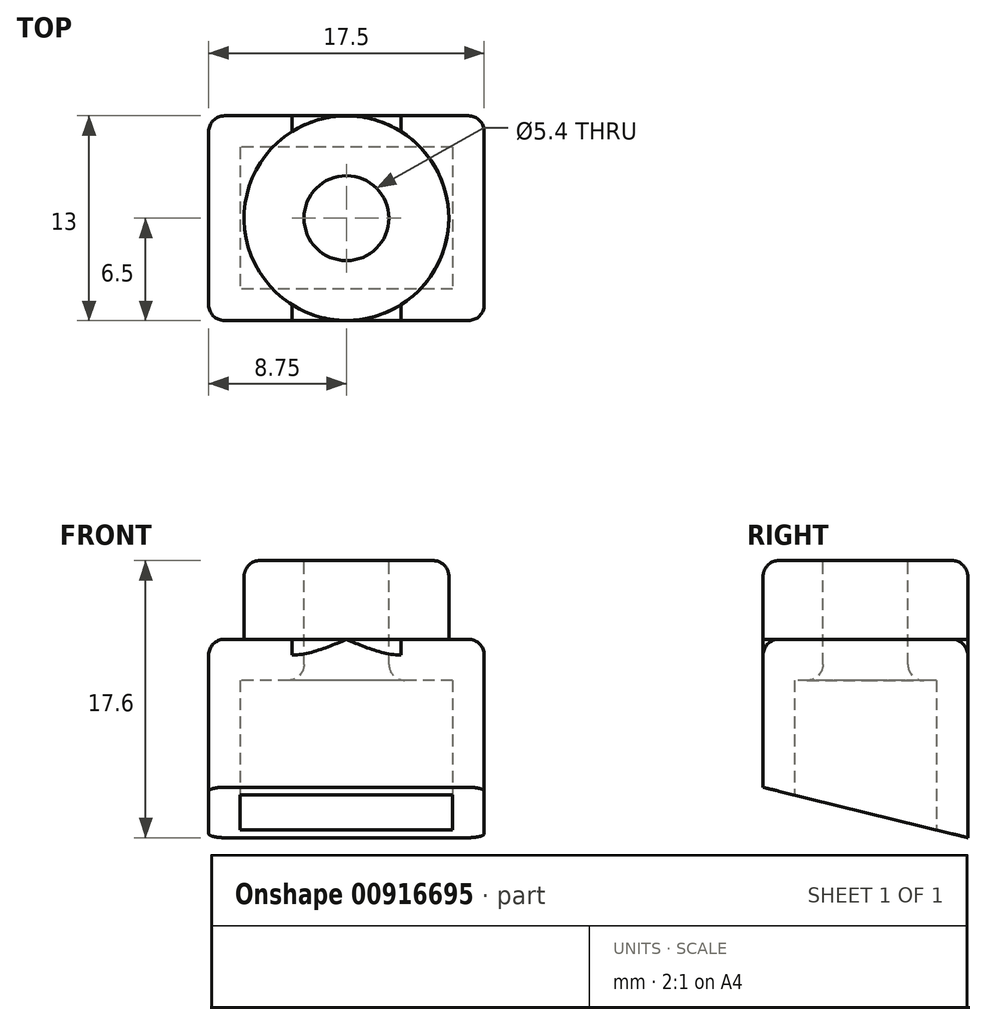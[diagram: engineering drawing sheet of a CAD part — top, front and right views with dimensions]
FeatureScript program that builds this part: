
annotation { "Feature Type Name" : "Feature", "Feature Type Description" : "" }
export const myFeature = defineFeature(function(context is Context, id is Id, definition is map)
    precondition{}
    {
        {
            var Q0;
            Q0=qCreatedBy(makeId("Top.planeOp"),FACE);
            var sketch = newSketch(context, id + "F0", { "sketchPlane" : qUnion([Q0])});
            skLineSegment(sketch, "E0.bottom", {"start": v(8.75, -6.5) * mm, "end": v(-8.75, -6.5) * mm});
            skLineSegment(sketch, "E0.top", {"start": v(8.75, 6.5) * mm, "end": v(-8.75, 6.5) * mm});
            skLineSegment(sketch, "E0.left", {"start": v(8.75, -6.5) * mm, "end": v(8.75, 6.5) * mm});
            skLineSegment(sketch, "E0.right", {"start": v(-8.75, -6.5) * mm, "end": v(-8.75, 6.5) * mm});
            skPoint(sketch, "E0.middle", {"position": v(0, 0) * mm});
            skSolve(sketch);
        }
        {
            var Q0;
            Q0 = qSketchRegion(id + "F0", true);
            extrude(context, id + "F1", {"entities" : qUnion([Q0]), "depth" : 12.6 * mm, "offsetDistance" : 25 * mm});
        }
        {
            var Q0;
            Q0=makeQuery(id+"F1.opExtrude","CAP_FACE",FACE,{"disambiguationData":[OSD([sQuery(id+"F0.wireOp",EDGE,"E0.bottom"),sQuery(id+"F0.wireOp",EDGE,"E0.top"),sQuery(id+"F0.wireOp",EDGE,"E0.left"),sQuery(id+"F0.wireOp",EDGE,"E0.right")])],"isStart":false});
            var sketch = newSketch(context, id + "F2", { "sketchPlane" : qUnion([Q0])});
            skCircle(sketch, "E1", {"center": v(0, 0) * mm, "radius": 6.5 * mm});
            skSolve(sketch);
        }
        {
            var Q0;
            Q0 = qSketchRegion(id + "F2", true);
            extrude(context, id + "F3", {"entities" : qUnion([Q0]), "operationType" : NewBodyOperationType.ADD, "depth" : 5 * mm, "offsetDistance" : 25 * mm});
        }
        {
            var Q0;
            Q0=makeQuery(id+"F1.opExtrude","SWEPT_FACE",FACE,{"disambiguationData":[OSD([sQuery(id+"F0.wireOp",EDGE,"E0.right")])]});
            var sketch = newSketch(context, id + "F4", { "sketchPlane" : qUnion([Q0])});
            skLineSegment(sketch, "E2", {"start": v(-6.5, 0) * mm, "end": v(6.5, 3.2) * mm});
            skLineSegment(sketch, "E3", {"start": v(6.5, 3.2) * mm, "end": v(6.5, 0) * mm});
            skLineSegment(sketch, "E4", {"start": v(6.5, 0) * mm, "end": v(-6.5, 0) * mm});
            skSolve(sketch);
        }
        {
            var Q0;
            Q0 = qSketchRegion(id + "F4", true);
            extrude(context, id + "F5", {"entities" : qUnion([Q0]), "operationType" : NewBodyOperationType.REMOVE, "endBound" : BoundingType.THROUGH_ALL, "oppositeDirection" : true, "depth" : 25 * mm, "offsetDistance" : 25 * mm});
        }
        {
            var Q0;
            Q0=makeQuery(id+"F3.opExtrude","CAP_FACE",FACE,{"disambiguationData":[OSD([sQuery(id+"F2.wireOp",EDGE,"E1")])],"isStart":false});
            var sketch = newSketch(context, id + "F6", { "sketchPlane" : qUnion([Q0])});
            skCircle(sketch, "E5", {"center": v(0, 0) * mm, "radius": 2.7 * mm});
            skSolve(sketch);
        }
        {
            var Q0;
            Q0 = qSketchRegion(id + "F6", true);
            extrude(context, id + "F7", {"entities" : qUnion([Q0]), "operationType" : NewBodyOperationType.REMOVE, "endBound" : BoundingType.THROUGH_ALL, "oppositeDirection" : true, "depth" : 25 * mm, "offsetDistance" : 25 * mm});
        }
        {
            var Q0;
            Q0=qCreatedBy(makeId("Top.planeOp"),FACE);
            var sketch = newSketch(context, id + "F8", { "sketchPlane" : qUnion([Q0])});
            skLineSegment(sketch, "E6.bottom", {"start": v(6.75, 4.5) * mm, "end": v(-6.75, 4.5) * mm});
            skLineSegment(sketch, "E6.top", {"start": v(6.75, -4.5) * mm, "end": v(-6.75, -4.5) * mm});
            skLineSegment(sketch, "E6.left", {"start": v(6.75, 4.5) * mm, "end": v(6.75, -4.5) * mm});
            skLineSegment(sketch, "E6.right", {"start": v(-6.75, 4.5) * mm, "end": v(-6.75, -4.5) * mm});
            skPoint(sketch, "E6.middle", {"position": v(0, 0) * mm});
            skSolve(sketch);
        }
        {
            var Q0;
            Q0 = qSketchRegion(id + "F8", true);
            extrude(context, id + "F9", {"entities" : qUnion([Q0]), "operationType" : NewBodyOperationType.REMOVE, "depth" : 10 * mm, "offsetDistance" : 25 * mm});
        }
        {
            var Q0;
            Q0=makeQuery(id+"F7.boolean.opBoolean","COPY",EDGE,{"derivedFrom":makeQuery(id+"F7.opExtrude","CAP_EDGE",EDGE,{"disambiguationData":[OSD([sQuery(id+"F6.wireOp",EDGE,"E5")])],"isStart":true})});
            var Q1;
            Q1=makeQuery(id+"F3.opExtrude","CAP_EDGE",EDGE,{"disambiguationData":[OSD([sQuery(id+"F2.wireOp",EDGE,"E1")])],"isStart":false});
            var Q2;
            {var subQ0=sQuery(id+"F0.wireOp",EDGE,"E0.right");var subQ1=sQuery(id+"F0.wireOp",EDGE,"E0.top");Q2=makeQuery(id+"F3.boolean.opBoolean","SPLIT",EDGE,{"disambiguationData":[TD([makeQuery(id+"F1.opExtrude","SWEPT_FACE",FACE,{"disambiguationData":[OSD([subQ0])]})])],"derivedFrom":makeQuery(id+"F1.opExtrude","CAP_EDGE",EDGE,{"disambiguationData":[OSD([subQ1])],"isStart":false})});}
            var Q3;
            Q3=makeQuery(id+"F1.opExtrude","CAP_EDGE",EDGE,{"disambiguationData":[OSD([sQuery(id+"F0.wireOp",EDGE,"E0.right")])],"isStart":false});
            var Q4;
            {var subQ0=sQuery(id+"F0.wireOp",EDGE,"E0.bottom");var subQ1=sQuery(id+"F0.wireOp",EDGE,"E0.right");Q4=makeQuery(id+"F3.boolean.opBoolean","SPLIT",EDGE,{"disambiguationData":[TD([makeQuery(id+"F1.opExtrude","SWEPT_FACE",FACE,{"disambiguationData":[OSD([subQ1])]})])],"derivedFrom":makeQuery(id+"F1.opExtrude","CAP_EDGE",EDGE,{"disambiguationData":[OSD([subQ0])],"isStart":false})});}
            var Q5;
            Q5=makeQuery(id+"F1.opExtrude","SWEPT_EDGE",EDGE,{"disambiguationData":[OSD([sQuery(id+"F0.wireOp",EDGE,"E0.top"),sQuery(id+"F0.wireOp",EDGE,"E0.right")])]});
            var Q6;
            Q6=makeQuery(id+"F1.opExtrude","SWEPT_EDGE",EDGE,{"disambiguationData":[OSD([sQuery(id+"F0.wireOp",EDGE,"E0.bottom"),sQuery(id+"F0.wireOp",EDGE,"E0.right")])]});
            var Q7;
            Q7=makeQuery(id+"F1.opExtrude","SWEPT_EDGE",EDGE,{"disambiguationData":[OSD([sQuery(id+"F0.wireOp",EDGE,"E0.bottom"),sQuery(id+"F0.wireOp",EDGE,"E0.left")])]});
            var Q8;
            Q8=makeQuery(id+"F1.opExtrude","SWEPT_EDGE",EDGE,{"disambiguationData":[OSD([sQuery(id+"F0.wireOp",EDGE,"E0.top"),sQuery(id+"F0.wireOp",EDGE,"E0.left")])]});
            var Q9;
            Q9=makeQuery(id+"F1.opExtrude","CAP_EDGE",EDGE,{"disambiguationData":[OSD([sQuery(id+"F0.wireOp",EDGE,"E0.left")])],"isStart":false});
            var Q10;
            Q10=makeQuery(id+"F9.boolean.opBoolean","INTERSECT",EDGE,{"derivedFrom":[makeQuery(id+"F7.boolean.opBoolean","COPY",FACE,{"derivedFrom":makeQuery(id+"F7.opExtrude","SWEPT_FACE",FACE,{"disambiguationData":[OSD([sQuery(id+"F6.wireOp",EDGE,"E5")])]})}),makeQuery(id+"F9.opExtrude","CAP_FACE",FACE,{"disambiguationData":[OSD([sQuery(id+"F8.wireOp",EDGE,"E6.bottom"),sQuery(id+"F8.wireOp",EDGE,"E6.top"),sQuery(id+"F8.wireOp",EDGE,"E6.left"),sQuery(id+"F8.wireOp",EDGE,"E6.right")])],"isStart":false})]});
            fillet(context, id + "F10", {"entities" : qUnion([Q0, Q1, Q2, Q3, Q4, Q5, Q6, Q7, Q8, Q9, Q10]), "radius" : 1 * mm, "tangentPropagation" : true, "allowEdgeOverflow" : false});
        }
    });
